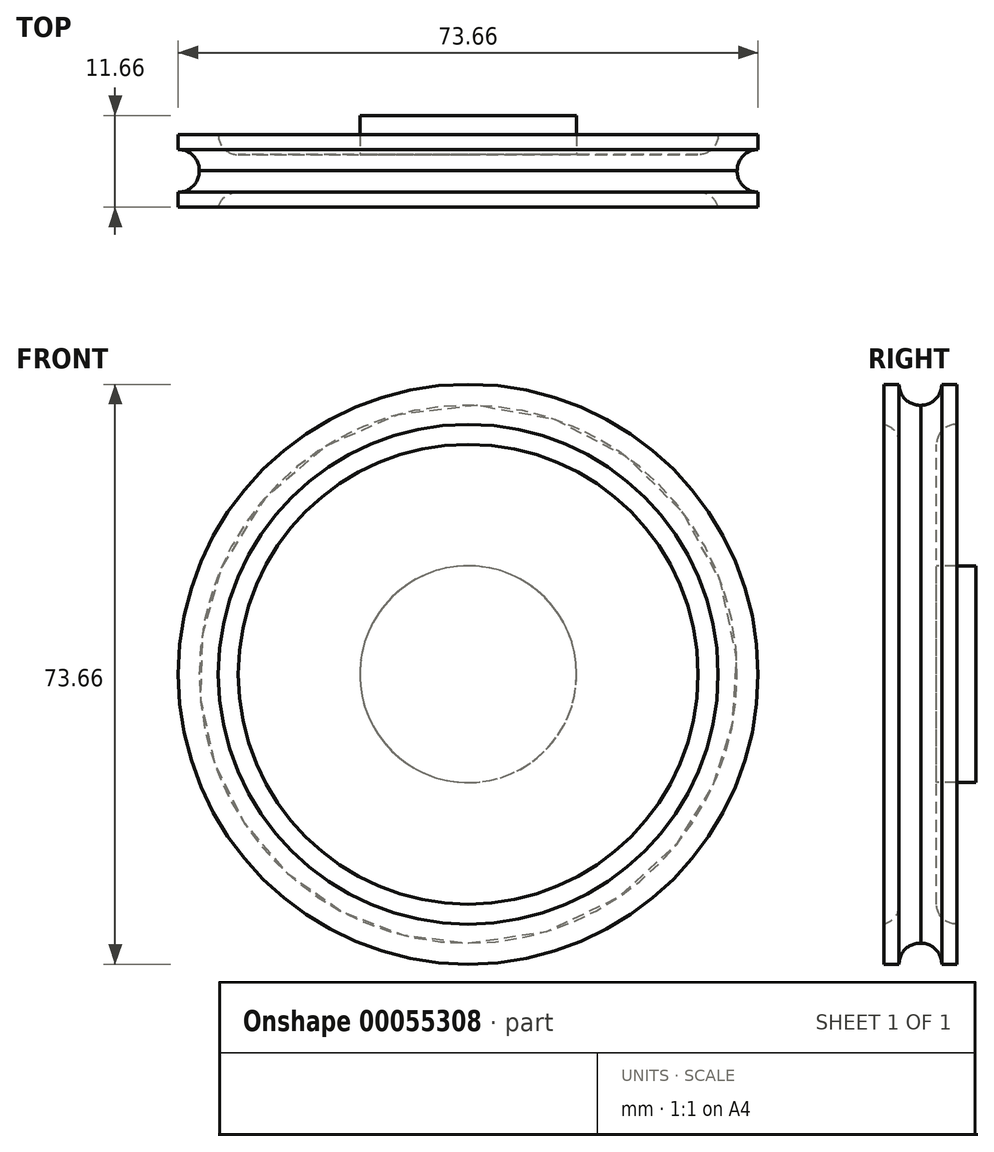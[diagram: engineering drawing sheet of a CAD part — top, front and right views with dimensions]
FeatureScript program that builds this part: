
annotation { "Feature Type Name" : "Feature", "Feature Type Description" : "" }
export const myFeature = defineFeature(function(context is Context, id is Id, definition is map)
    precondition{}
    {
        {
            var Q0;
            Q0=qCreatedBy(makeId("Right.planeOp"),FACE);
            var sketch = newSketch(context, id + "F0", { "sketchPlane" : qUnion([Q0])});
            skLineSegment(sketch, "E0", {"start": v(0, 0) * mm, "end": v(0, 29.21) * mm});
            skArc(sketch, "E1", {"start": v(0, 29.21) * mm, "mid": v(0.76, 31.02) * mm, "end": v(2.57, 31.75) * mm});
            skLineSegment(sketch, "E2", {"start": v(2.57, 31.75) * mm, "end": v(2.57, 36.83) * mm});
            skLineSegment(sketch, "E3", {"start": v(2.57, 36.83) * mm, "end": v(0.67, 36.83) * mm});
            skArc(sketch, "E4", {"start": v(-2, 34.16) * mm, "mid": v(-0.11, 34.94) * mm, "end": v(0.67, 36.83) * mm});
            skArc(sketch, "E5", {"start": v(-4.76, 36.83) * mm, "mid": v(-3.95, 34.91) * mm, "end": v(-2, 34.16) * mm});
            skLineSegment(sketch, "E6", {"start": v(-4.76, 36.83) * mm, "end": v(-6.66, 36.83) * mm});
            skLineSegment(sketch, "E7", {"start": v(-6.66, 36.83) * mm, "end": v(-6.66, 31.75) * mm});
            skArc(sketch, "E8", {"start": v(-4.76, 29.21) * mm, "mid": v(-5.27, 30.81) * mm, "end": v(-6.66, 31.75) * mm});
            skLineSegment(sketch, "E9", {"start": v(-4.76, 29.21) * mm, "end": v(-4.76, 0) * mm});
            skLineSegment(sketch, "E10", {"start": v(-4.76, 0) * mm, "end": v(0, 0) * mm});
            skSolve(sketch);
        }
        {
            var Q0;
            Q0=makeQuery(id+"F0.imprint","IMPRINT",FACE,{"disambiguationData":[TD([[makeQuery(id+"F0.imprint","IMPRINT",EDGE,{"derivedFrom":sQuery(id+"F0.wireOp",EDGE,"E0")}),1.0]])]});
            var Q1;
            Q1=sQuery(id+"F0.wireOp",EDGE,"E10");
            revolve(context, id + "F1", {"entities" : qUnion([Q0]), "axis" : qUnion([Q1]), "revolveType" : RevolveType.FULL});
        }
        {
            var Q0;
            Q0=makeQuery(id+"F1.opRevolve","SWEPT_FACE",FACE,{"disambiguationData":[OSD([sQuery(id+"F0.wireOp",EDGE,"E0")])]});
            var sketch = newSketch(context, id + "F2", { "sketchPlane" : qUnion([Q0])});
            skCircle(sketch, "E11", {"center": v(0, 0) * mm, "radius": 13.77 * mm});
            skSolve(sketch);
        }
        {
            var Q0;
            Q0 = qSketchRegion(id + "F2", true);
            extrude(context, id + "F3", {"entities" : qUnion([Q0]), "operationType" : NewBodyOperationType.ADD, "depth" : 5 * mm});
        }
    });
